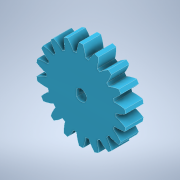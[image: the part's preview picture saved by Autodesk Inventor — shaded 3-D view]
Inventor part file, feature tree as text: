
AUTODESK INVENTOR PART (.ipt)
format: ipt  version: 2022.2 (Build 262287010, 287A)  size: 297,472 bytes
history: native  units: mm (DEFAULTED — no unit token found)
features: sketch x5, extrude x4, plane x3, other x3
ambient origin geometry x8: Origin, YZ Plane, XZ Plane, XY Plane, X Axis, Y Axis, Z Axis, Center Point
bodies: Solid1 (feature_tree)
feature tree (15):
  extrude  "Extrusion1"  Depth=8.0mm TaperAngle=0.0deg
  plane  "Work Plane2"
  plane  "Work Plane8"
  plane  "Work Plane9"
  other  "Engranaje recto"
  extrude  "Extrusión2"  Depth=10.0mm TaperAngle=0.0deg
  extrude  "Extrusión4"  Depth=1.745329mm TaperAngle=0.0deg
  extrude  "Extrusión5"  TaperAngle=0.0deg  [1 undecoded]
  sketch  "Sketch1"  dims[d0=40.0mm d1=8.0mm d2=0.0mm]
  sketch  "Sketch2"  dims[d3=36.0mm d4=10.0mm d5=0.0mm]
  other  "Srf1"
  sketch  "Boceto3"  dims[d16=90.0mm d17=0.0mm d34=1.745329mm]
  sketch  "Boceto6"  dims[d39=0.0mm d41=0.0mm]
  sketch  "Boceto8"  dims[d43=90.0mm d46=90.0mm d47=0.0mm d48=0.0mm d49=5.0mm d50=0.0mm d51=0.0mm d56=8.0mm d57=0.0mm d58=2.5mm d59=0.0mm d60=0.0mm d61=0.5mm d62=0.872665mm d63=0.5mm d64=0.872665mm]
  other  "Diámetro de separación"
note: 1 required parameter value undecoded (feature->parameter linkage not recoverable at this tier; creation-order binding heuristic only, values carry confidence <= 0.55)
